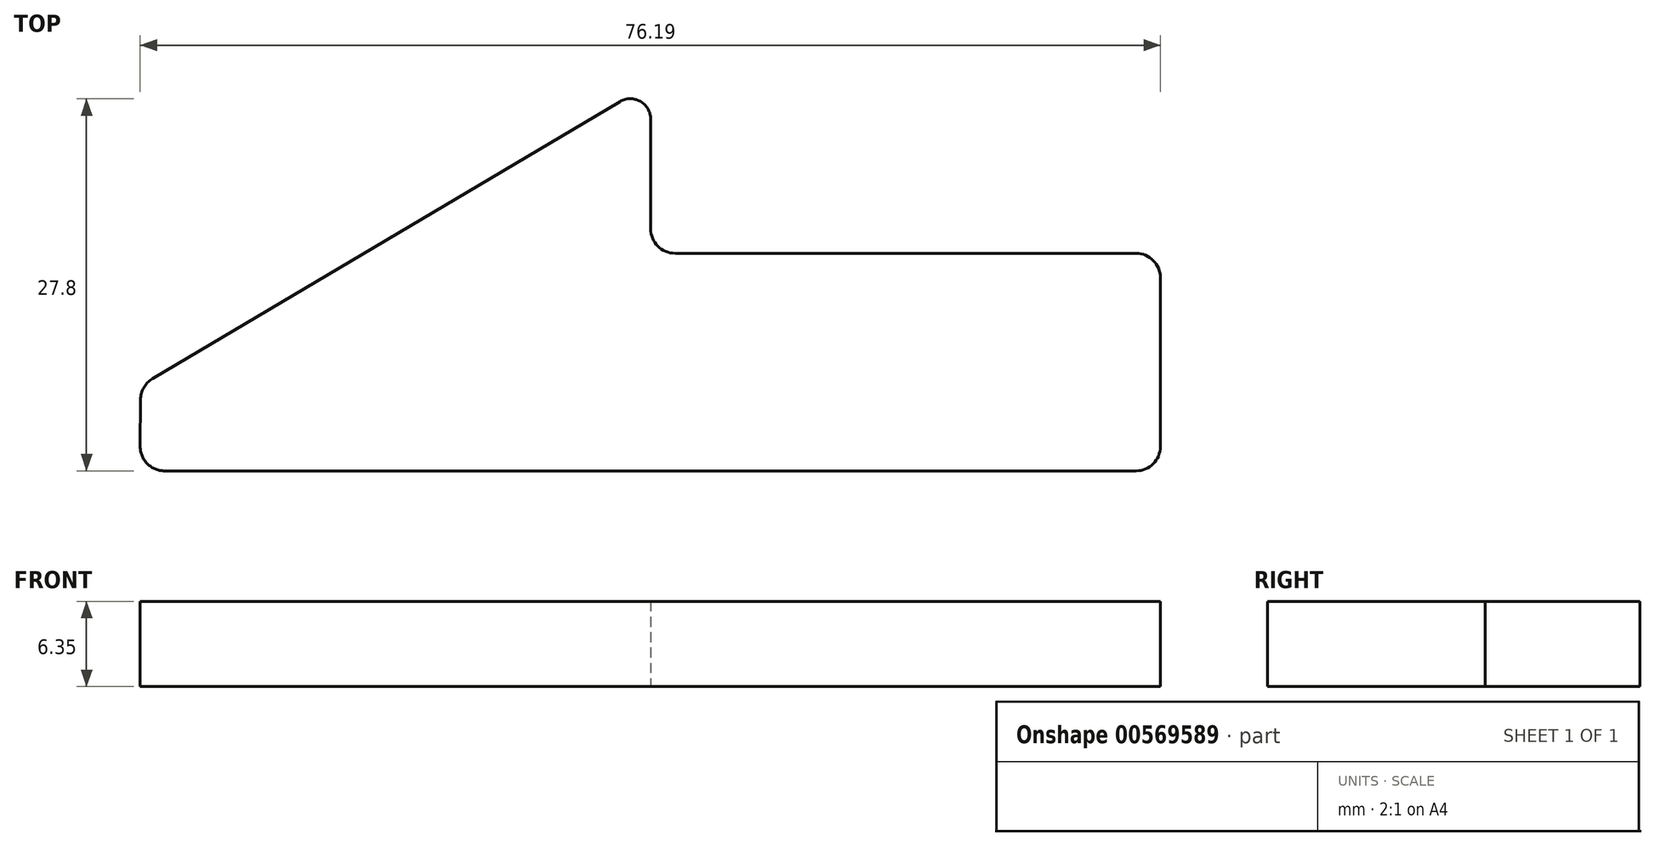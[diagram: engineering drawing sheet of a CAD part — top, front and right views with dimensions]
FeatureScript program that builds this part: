
annotation { "Feature Type Name" : "Feature", "Feature Type Description" : "" }
export const myFeature = defineFeature(function(context is Context, id is Id, definition is map)
    precondition{}
    {
        {
            var Q0;
            Q0=qCreatedBy(makeId("Top.planeOp"),FACE);
            var sketch = newSketch(context, id + "F0", { "sketchPlane" : qUnion([Q0])});
            skLineSegment(sketch, "E0", {"start": v(0.04, 6.35) * mm, "end": v(35.83, 27.6) * mm});
            skLineSegment(sketch, "E1", {"start": v(38.14, 26.28) * mm, "end": v(38.14, 16.26) * mm});
            skLineSegment(sketch, "E2", {"start": v(38.14, 16.26) * mm, "end": v(76.2, 16.26) * mm});
            skLineSegment(sketch, "E3", {"start": v(76.2, 16.26) * mm, "end": v(76.2, 0) * mm});
            skLineSegment(sketch, "E4", {"start": v(76.2, 0) * mm, "end": v(0, 0) * mm});
            skLineSegment(sketch, "E5", {"start": v(0, 0) * mm, "end": v(0.04, 6.35) * mm});
            skPoint(sketch, "E6.visualSharp", {"position": v(38.14, 28.96) * mm});
            skArc(sketch, "E6.filletArc", {"start": v(38.14, 26.28) * mm, "mid": v(37.37, 27.6) * mm, "end": v(35.83, 27.6) * mm});
            skLineSegment(sketch, "E7", {"start": v(0.04, 6.35) * mm, "end": v(0.04, 61.49) * mm, "construction": true});
            skSolve(sketch);
        }
        {
            var Q0;
            Q0=makeQuery(id+"F0.imprint","IMPRINT",FACE,{"disambiguationData":[TD([[makeQuery(id+"F0.imprint","IMPRINT",EDGE,{"derivedFrom":sQuery(id+"F0.wireOp",EDGE,"E0")}),-1.0]])]});
            extrude(context, id + "F1", {"entities" : qUnion([Q0]), "depth" : 6.35 * mm, "offsetDistance" : 25.4 * mm});
        }
        {
            var Q0;
            Q0=makeQuery(id+"F1.opExtrude","SWEPT_EDGE",EDGE,{"disambiguationData":[OSD([sQuery(id+"F0.wireOp",EDGE,"E0"),sQuery(id+"F0.wireOp",EDGE,"E5")])]});
            var Q1;
            Q1=makeQuery(id+"F1.opExtrude","SWEPT_EDGE",EDGE,{"disambiguationData":[OSD([sQuery(id+"F0.wireOp",EDGE,"E3"),sQuery(id+"F0.wireOp",EDGE,"E4")])]});
            var Q2;
            Q2=makeQuery(id+"F1.opExtrude","SWEPT_EDGE",EDGE,{"disambiguationData":[OSD([sQuery(id+"F0.wireOp",EDGE,"E2"),sQuery(id+"F0.wireOp",EDGE,"E3")])]});
            var Q3;
            Q3=makeQuery(id+"F1.opExtrude","SWEPT_EDGE",EDGE,{"disambiguationData":[OSD([sQuery(id+"F0.wireOp",EDGE,"E1"),sQuery(id+"F0.wireOp",EDGE,"E2")])]});
            var Q4;
            Q4=makeQuery(id+"F1.opExtrude","SWEPT_EDGE",EDGE,{"disambiguationData":[OSD([sQuery(id+"F0.wireOp",EDGE,"E4"),sQuery(id+"F0.wireOp",EDGE,"E5")])]});
            fillet(context, id + "F2", {"entities" : qUnion([Q0, Q1, Q2, Q3, Q4]), "radius" : 1.82 * mm, "tangentPropagation" : true, "allowEdgeOverflow" : false});
        }
    });
